FCSTD DOCUMENT  (FreeCAD 0.20RUnknown)
Label: boks
License: All rights reserved
LicenseURL: http://en.wikipedia.org/wiki/All_rights_reserved
objects: Sketcher::SketchObject×1, PartDesign::Body×1, Spreadsheet::Sheet×1
note: 2 computed .brp shape members not serialized (recipe doc carries the construction recipe); baked Part::Feature solids carry a one-line shape summary decoded from their .brp

FEATURE [Sketcher::SketchObject] Sketch
  FullyConstrained = true
  MapMode = 5
  Support = -> [XY_Plane]
  expr: Constraints[12] = Spreadsheet.box_width
  expr: Constraints[13] = Spreadsheet.box_length
  expr: Constraints[17] = <<Spreadsheet>>.box_outer_arc_radius
  expr: Constraints[31] = <<Spreadsheet>>.box_inner_arc_radius
  expr: Constraints[36] = <<Spreadsheet>>.box_inner_length
  expr: Constraints[37] = <<Spreadsheet>>.box_inner_width
  expr: Constraints[47] = <<Spreadsheet>>.box_inner_length / 2 - <<Spreadsheet>>.hole_from_edge_x
  expr: Constraints[48] = <<Spreadsheet>>.box_inner_width / 2 - Spreadsheet.hole_from_edge_y
  sketch-geometry (20):
    g0: LineSegment StartX=-70 StartY=50 StartZ=0 EndX=70 EndY=50 EndZ=0
    g1: LineSegment StartX=75 StartY=45 StartZ=0 EndX=75 EndY=-45 EndZ=0
    g2: LineSegment StartX=70 StartY=-50 StartZ=0 EndX=-70 EndY=-50 EndZ=0
    g3: LineSegment StartX=-75 StartY=-45 StartZ=0 EndX=-75 EndY=45 EndZ=0
    g4: ArcOfCircle CenterX=-70 CenterY=45 CenterZ=0 NormalX=0 NormalY=0 NormalZ=1 AngleXU=0 Radius=5 StartAngle=1.5708 EndAngle=3.14159
    g5: ArcOfCircle CenterX=70 CenterY=45 CenterZ=0 NormalX=0 NormalY=0 NormalZ=1 AngleXU=0 Radius=5 StartAngle=3e-16 EndAngle=1.5708
    g6: ArcOfCircle CenterX=70 CenterY=-45 CenterZ=0 NormalX=0 NormalY=0 NormalZ=1 AngleXU=0 Radius=5 StartAngle=4.71239 EndAngle=6.28319
    g7: ArcOfCircle CenterX=-70 CenterY=-45 CenterZ=0 NormalX=0 NormalY=0 NormalZ=1 AngleXU=0 Radius=5 StartAngle=3.14159 EndAngle=4.71239
    g8: LineSegment StartX=-70.5 StartY=47.5 StartZ=0 EndX=70.5 EndY=47.5 EndZ=0
    g9: LineSegment StartX=72.5 StartY=45.5 StartZ=0 EndX=72.5 EndY=-45.5 EndZ=0
    g10: LineSegment StartX=70.5 StartY=-47.5 StartZ=0 EndX=-70.5 EndY=-47.5 EndZ=0
    g11: LineSegment StartX=-72.5 StartY=-45.5 StartZ=0 EndX=-72.5 EndY=45.5 EndZ=0
    g12: ArcOfCircle CenterX=-70.5 CenterY=45.5 CenterZ=0 NormalX=0 NormalY=0 NormalZ=1 AngleXU=0 Radius=2 StartAngle=1.5708 EndAngle=3.14159
    g13: ArcOfCircle CenterX=70.5 CenterY=45.5 CenterZ=0 NormalX=0 NormalY=0 NormalZ=1 AngleXU=0 Radius=2 StartAngle=-9e-16 EndAngle=1.5708
    g14: ArcOfCircle CenterX=70.5 CenterY=-45.5 CenterZ=0 NormalX=0 NormalY=0 NormalZ=1 AngleXU=0 Radius=2 StartAngle=4.71239 EndAngle=6.28319
    g15: ArcOfCircle CenterX=-70.5 CenterY=-45.5 CenterZ=0 NormalX=0 NormalY=0 NormalZ=1 AngleXU=0 Radius=2 StartAngle=3.14159 EndAngle=4.71239
    g16: LineSegment StartX=-72.5 StartY=47.5 StartZ=0 EndX=-62.5 EndY=47.5 EndZ=0
    g17: LineSegment StartX=-72.5 StartY=47.5 StartZ=0 EndX=-72.5 EndY=37.5 EndZ=0
    g18: ArcOfCircle CenterX=-72.5 CenterY=47.5 CenterZ=0 NormalX=0 NormalY=0 NormalZ=1 AngleXU=0 Radius=10 StartAngle=4.71239 EndAngle=6.28319
    g19: Circle CenterX=-67.5 CenterY=42.5 CenterZ=0 NormalX=0 NormalY=0 NormalZ=1 AngleXU=0 Radius=1.255
  constraints (49):
    c: Horizontal(g0)
    c: Horizontal(g2)
    c: Vertical(g1)
    c: Vertical(g3)
    c: Tangent(g3,g4) = 1.5708
    c: Tangent(g0,g4) = 1.5708
    c: Tangent(g0,g5) = 1.5708
    c: Tangent(g1,g5) = 1.5708
    c: Tangent(g1,g6) = 1.5708
    c: Tangent(g2,g6) = 1.5708
    c: Tangent(g2,g7) = 1.5708
    c: Tangent(g3,g7) = 1.5708
    c: DistanceY(g2,g0) = 100
    c: DistanceX(g3,g1) = 150
    c: Equal(g7,g4)
    c: Equal(g4,g5)
    c: Equal(g5,g6)
    c: Radius(g4) = 5
    c: Symmetric(g4,g6,g-1)
    c: Horizontal(g8)
    c: Horizontal(g10)
    c: Vertical(g9)
    c: Vertical(g11)
    c: Tangent(g11,g12) = 1.5708
    c: Tangent(g8,g12) = 1.5708
    c: Tangent(g8,g13) = 1.5708
    c: Tangent(g9,g13) = 1.5708
    c: Tangent(g9,g14) = 1.5708
    c: Tangent(g10,g14) = 1.5708
    c: Tangent(g10,g15) = 1.5708
    c: Tangent(g11,g15) = 1.5708
    c: Radius(g12) = 2
    c: Equal(g13,g12)
    c: Equal(g12,g15)
    c: Equal(g15,g14)
    c: Symmetric(g12,g14,g-1)
    c: DistanceX(g11,g9) = 145
    c: DistanceY(g10,g8) = 95
    c: Horizontal(g16)
    c: Coincident(g17,g16)
    c: Vertical(g17)
    c: Coincident(g18,g16)
    c: Coincident(g18,g17)
    c: Coincident(g18,g16)
    c: Radius(g18) = 10
    c: Symmetric(g16,g17,g19)
    c: Diameter(g19) = 2.51
    c: DistanceX(g19,g-1) = 67.5
    c: DistanceY(g-1,g19) = 42.5
FEATURE [PartDesign::Body] Body
  Group = -> [Sketch]
  Origin = -> Origin
FEATURE [Spreadsheet::Sheet] Spreadsheet
  cells = A1=box_length; B1(box_length)=150; A2=box_width; B2(box_width)=100; A3=hose_hole_width; B3(hose_hole_width)=44.6; A4=hose_hole_length; B4(hose_hole_length)=39.4; A5=box_wall_thickness; B5=10; A6=box_inner_width; B6(box_inner_width)==B2 - B5 / 2; A7=box_inner_length; B7(box_inner_length)==B1 - B5 / 2; A8=box_inner_arc_radius; B8(box_inner_arc_radius)=2; A9=box_outer_arc_radius; B9(box_outer_arc_radius)=5; A10=hole_from_edge_x; B10(hole_from_edge_x)=5; A11=hole_from_edge_y; B11(hole_from_edge_y)=5
